# Revit family: IS_PrivoII_T2615_BIM_DE
name_source: partatom
category: Plumbing Fixtures
revit_build: Autodesk Revit MEP 2016 (Build: 20161004_0715(x64)
units: mm (PartAtom-declared; Revit-internal decimal feet)

## family parameters
Always vertical = No
Cut with Voids When Loaded = No
OmniClass Number = 23.45.05.21.11.21
OmniClass Title = Urinals
Part Type = Normal
Room Calculation Point = No
Round Connector Dimension = Use Diameter
Shared = No
Work Plane-Based = No

## types (2) — shared parameters
Accessories = www.idealstandard.de\ersatzteile
AssetType = Fixed
BIMobject category = Urinals
BOSUseNativeGeometries = 1
Brand = Ideal Standard
Brand url = http://www.idealstandard.de
ConnectionType = Plumbing
CurrencyUnit = €
CurrentRevision = 1
Date of publishing = 20/12/2017
DurationUnit = Year
Edition number = 1
ExpectedLife = 25
IFC Classification = Sanitary Terminal
IfcExportAs = IfcSanitaryTerminalType
Installation instructions = http://www.idealstandard.de
InstallationInstructions = www.idealstandard.de\produkte
MaintenanceInformation = www.idealstandard.de\produkte
Manufacturer name = Ideal Standard
ManufacturerURL = http://www.idealstandard.de
Material = Vitreous china
Material main = Ceramics
NettWeight = 10.5 Kg
Nominal height = 530
Nominal width = 300
NominalDepth = 292 mm
NominalHeight = 530 mm
NominalLength = 292 mm
NominalWidth = 301 mm
Product Guid = 0db02d01-24c9-4937-80e0-1b7ccbc7ab70
Product SKU = T2615
Product data url = https://bimobject.com
Product family = Sanitary
Product group = Urinal
Product name = PRIVO II urinal 300x290mm, back inlet
Product url = http://www.idealstandard.de
ProductInformation = www.idealstandard.de/produkte
QR code = http://bimobject.com
Shape = Sculptured
Size = 530x 292 x 301mm
Space = Internal
SpareParts = www.idealstandard.de/ersatzteile
Technical description = http://www.idealstandard.de
URL = http://www.idealstandard.de
Uniclass2015Code = Pr_40_20_93_82
Uniclass2015Title = Wall-hung urinals
Uniclass2015Version = Products v1.1
Version = 1
VolumeUnits = Litres
Weight Net (Kg) = 10.5
zero-valued in all types: Cost

## per-type parameters (varying)
| type | BIMObjectName | BarCode | CodePerformance | Color | Description | EAN code | Features | Finish | MainColor | Model | ModelNumber | ModelReference | Name |
| T261501 - PRIVO II urinal 300x290mm, back inlet | ISI_IdealStandard_Wall-HungUrinals_PrivoII_T261501 | 8014140410928 | DIN EN 997 | White | IS Absaugeurinal PRIVO II, Zulauf v.hi., 300x290x530mm, Weiß | https://8014140410928 | IS Absaugeurinal PRIVO II, Zulauf v.hi., 300x290x530mm, Weiß | White | White | T261501 | T261501 | IS Absaugeurinal PRIVO II, Zulauf v.hi., 300x290x530mm, Weiß | Wall-HungUrinals_PrivoII_T261501 |
| T2615MA - PRIVO II urinal 300x290mm, back inlet | ISI_IdealStandard_Wall-HungUrinals_PrivoII_T2615MA | 8014140410935 | 0 | WHITE IP | IS Absaugeurinal PRIVO II, Zulauf v.hi., 300x290x530mm, Weiß m.IP | https://8014140410935 | IS Absaugeurinal PRIVO II, Zulauf v.hi., 300x290x530mm, Weiß m.IP | WHITE IP | WHITE IP | T2615MA | T2615MA | IS Absaugeurinal PRIVO II, Zulauf v.hi., 300x290x530mm, Weiß m.IP | Wall-HungUrinals_PrivoII_T2615MA |

## geometry (parser evidence)
native form markers: Blend x4, Sweep x2
no freeform markers — native parametric forms only
